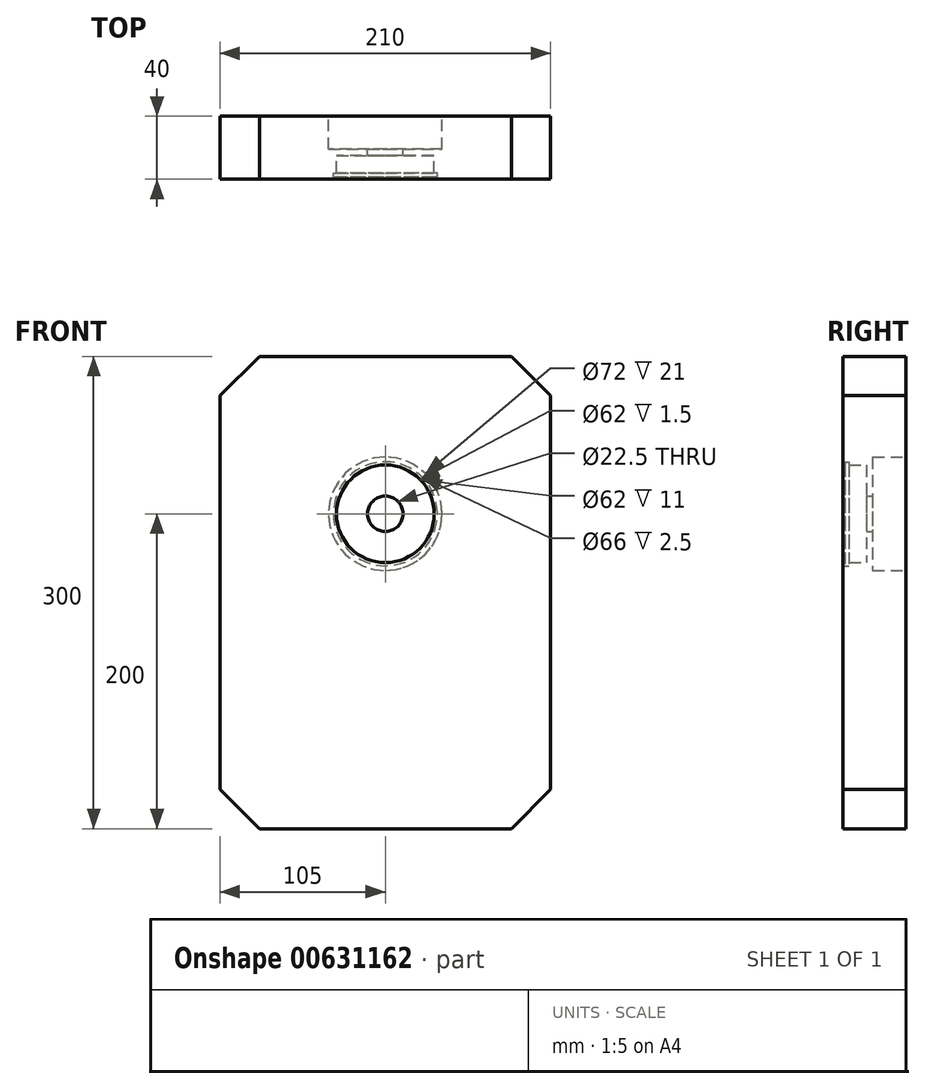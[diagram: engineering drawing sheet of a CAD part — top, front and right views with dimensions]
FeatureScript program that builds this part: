
annotation { "Feature Type Name" : "Feature", "Feature Type Description" : "" }
export const myFeature = defineFeature(function(context is Context, id is Id, definition is map)
    precondition{}
    {
        {
            var Q0;
            Q0=qCreatedBy(makeId("Front.planeOp"),FACE);
            var sketch = newSketch(context, id + "F0", { "sketchPlane" : qUnion([Q0])});
            skLineSegment(sketch, "E0.bottom", {"start": v(-80, 150) * mm, "end": v(80, 150) * mm});
            skLineSegment(sketch, "E0.top", {"start": v(-80, -150) * mm, "end": v(80, -150) * mm});
            skLineSegment(sketch, "E0.left", {"start": v(-105, 125) * mm, "end": v(-105, -125) * mm});
            skLineSegment(sketch, "E0.right", {"start": v(105, 125) * mm, "end": v(105, -125) * mm});
            skLineSegment(sketch, "E1", {"start": v(-80, 150) * mm, "end": v(-105, 125) * mm});
            skLineSegment(sketch, "E2", {"start": v(-105, -125) * mm, "end": v(-80, -150) * mm});
            skLineSegment(sketch, "E3", {"start": v(80, 150) * mm, "end": v(105, 125) * mm});
            skLineSegment(sketch, "E4", {"start": v(80, -150) * mm, "end": v(105, -125) * mm});
            skSolve(sketch);
        }
        {
            var Q0;
            Q0 = qSketchRegion(id + "F0", true);
            extrude(context, id + "F1", {"entities" : qUnion([Q0]), "endBound" : BoundingType.SYMMETRIC, "depth" : 40 * mm, "offsetDistance" : 25 * mm});
        }
        {
            var Q0;
            Q0=qCreatedBy(makeId("Right.planeOp"),FACE);
            var sketch = newSketch(context, id + "F2", { "sketchPlane" : qUnion([Q0])});
            skLineSegment(sketch, "E5", {"start": v(-53.7, 50) * mm, "end": v(65.04, 50) * mm, "construction": true});
            skLineSegment(sketch, "E6.bottom", {"start": v(-21.54, 50) * mm, "end": v(-18.5, 50) * mm});
            skLineSegment(sketch, "E6.top", {"start": v(-21.54, 81) * mm, "end": v(-18.5, 81) * mm});
            skLineSegment(sketch, "E6.left", {"start": v(-21.54, 50) * mm, "end": v(-21.54, 81) * mm});
            skLineSegment(sketch, "E6.right", {"start": v(-18.5, 50) * mm, "end": v(-18.5, 81) * mm});
            skLineSegment(sketch, "E7.bottom", {"start": v(-18.5, 50) * mm, "end": v(-16, 50) * mm});
            skLineSegment(sketch, "E7.top", {"start": v(-18.5, 83) * mm, "end": v(-16, 83) * mm});
            skLineSegment(sketch, "E7.left", {"start": v(-18.5, 50) * mm, "end": v(-18.5, 83) * mm});
            skLineSegment(sketch, "E7.right", {"start": v(-16, 50) * mm, "end": v(-16, 83) * mm});
            skLineSegment(sketch, "E8.bottom", {"start": v(-16, 50) * mm, "end": v(-5, 50) * mm});
            skLineSegment(sketch, "E8.top", {"start": v(-16, 81) * mm, "end": v(-5, 81) * mm});
            skLineSegment(sketch, "E8.left", {"start": v(-16, 50) * mm, "end": v(-16, 81) * mm});
            skLineSegment(sketch, "E8.right", {"start": v(-5, 50) * mm, "end": v(-5, 81) * mm});
            skLineSegment(sketch, "E9.bottom", {"start": v(-5, 50) * mm, "end": v(-1, 50) * mm});
            skLineSegment(sketch, "E9.top", {"start": v(-5, 61.25) * mm, "end": v(-1, 61.25) * mm});
            skLineSegment(sketch, "E9.left", {"start": v(-5, 50) * mm, "end": v(-5, 61.25) * mm});
            skLineSegment(sketch, "E9.right", {"start": v(-1, 50) * mm, "end": v(-1, 61.25) * mm});
            skLineSegment(sketch, "E10.bottom", {"start": v(-1, 50) * mm, "end": v(34.81, 50) * mm});
            skLineSegment(sketch, "E10.top", {"start": v(-1, 86) * mm, "end": v(34.81, 86) * mm});
            skLineSegment(sketch, "E10.left", {"start": v(-1, 50) * mm, "end": v(-1, 86) * mm});
            skLineSegment(sketch, "E10.right", {"start": v(34.81, 50) * mm, "end": v(34.81, 86) * mm});
            skSolve(sketch);
        }
        {
            var Q0;
            Q0 = qSketchRegion(id + "F2", true);
            var Q1;
            Q1=sQuery(id+"F2.wireOp",EDGE,"E5");
            revolve(context, id + "F3", {"operationType" : NewBodyOperationType.REMOVE, "entities" : qUnion([Q0]), "axis" : qUnion([Q1]), "revolveType" : RevolveType.FULL, "oppositeDirection" : true});
        }
    });
